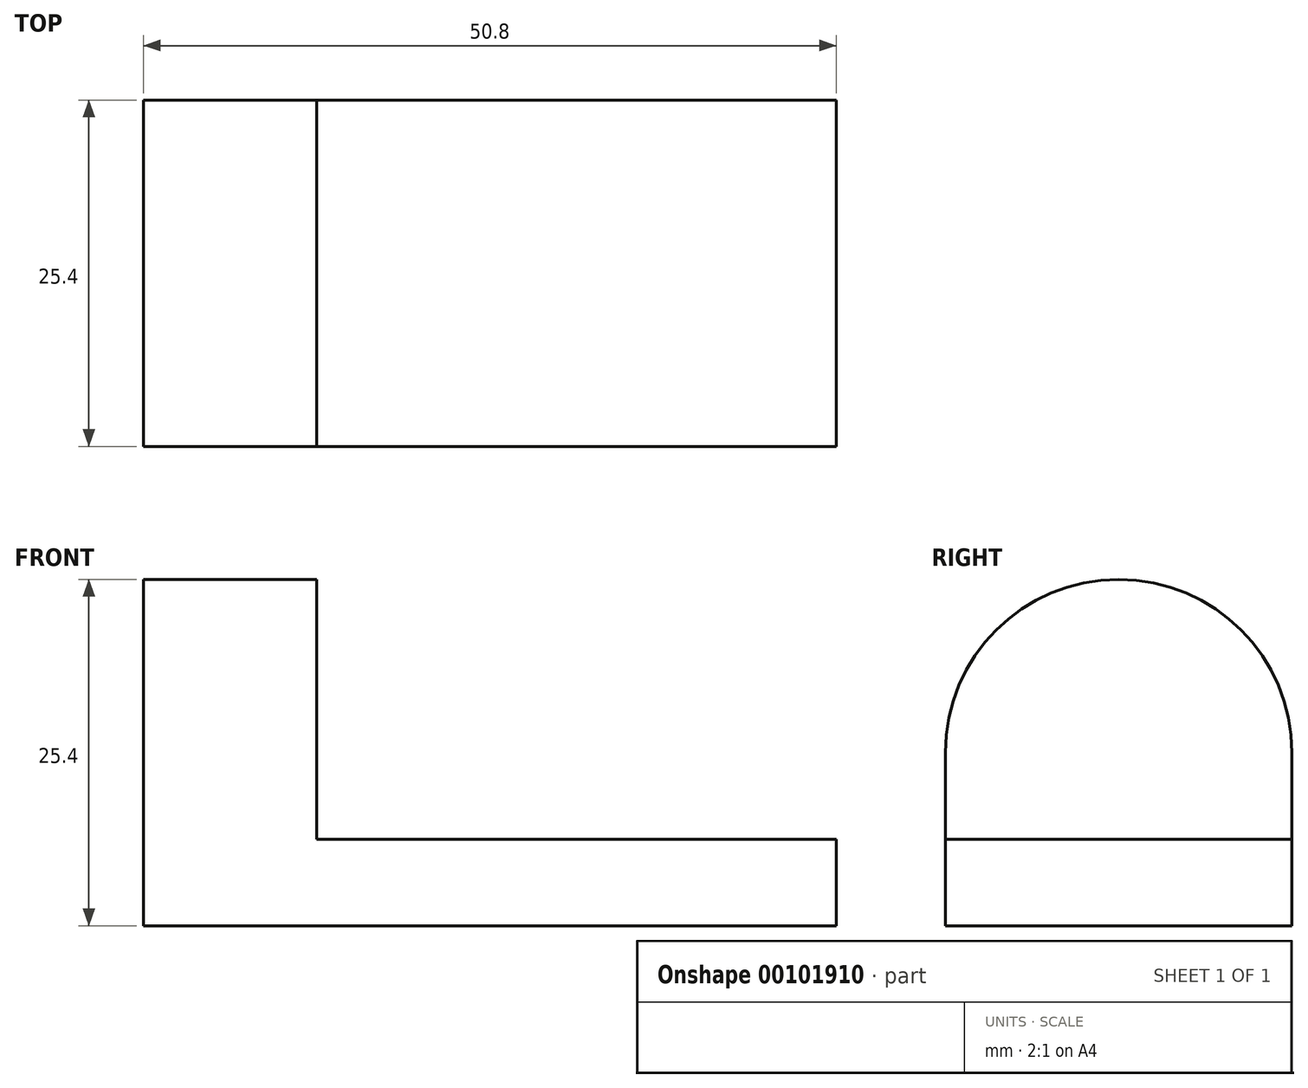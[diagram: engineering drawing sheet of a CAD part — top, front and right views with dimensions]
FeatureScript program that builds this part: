
annotation { "Feature Type Name" : "Feature", "Feature Type Description" : "" }
export const myFeature = defineFeature(function(context is Context, id is Id, definition is map)
    precondition{}
    {
        {
            var Q0;
            Q0=qCreatedBy(makeId("Front.planeOp"),FACE);
            var sketch = newSketch(context, id + "F0", { "sketchPlane" : qUnion([Q0])});
            skLineSegment(sketch, "E0.bottom", {"start": v(0, 0) * mm, "end": v(38.1, 0) * mm});
            skLineSegment(sketch, "E0.top", {"start": v(0, 6.35) * mm, "end": v(38.1, 6.35) * mm});
            skLineSegment(sketch, "E0.left", {"start": v(0, 0) * mm, "end": v(0, 6.35) * mm});
            skLineSegment(sketch, "E0.right", {"start": v(38.1, 0) * mm, "end": v(38.1, 6.35) * mm});
            skSolve(sketch);
        }
        {
            var Q0;
            Q0 = qSketchRegion(id + "F0", true);
            extrude(context, id + "F1", {"entities" : qUnion([Q0]), "depth" : 25.4 * mm});
        }
        {
            var Q0;
            Q0=makeQuery(id+"F1.opExtrude","SWEPT_FACE",FACE,{"disambiguationData":[OSD([sQuery(id+"F0.wireOp",EDGE,"E0.left")])]});
            var sketch = newSketch(context, id + "F2", { "sketchPlane" : qUnion([Q0])});
            skLineSegment(sketch, "E1", {"start": v(0, 0) * mm, "end": v(0, 12.7) * mm});
            skArc(sketch, "E2", {"start": v(25.4, 12.7) * mm, "mid": v(12.7, 25.4) * mm, "end": v(0, 12.7) * mm});
            skLineSegment(sketch, "E3", {"start": v(25.4, 12.7) * mm, "end": v(25.4, 0) * mm});
            skLineSegment(sketch, "E4", {"start": v(25.4, 0) * mm, "end": v(0, 0) * mm});
            skSolve(sketch);
        }
        {
            var Q0;
            Q0 = qSketchRegion(id + "F2", true);
            extrude(context, id + "F3", {"entities" : qUnion([Q0]), "operationType" : NewBodyOperationType.ADD, "depth" : 12.7 * mm});
        }
    });
